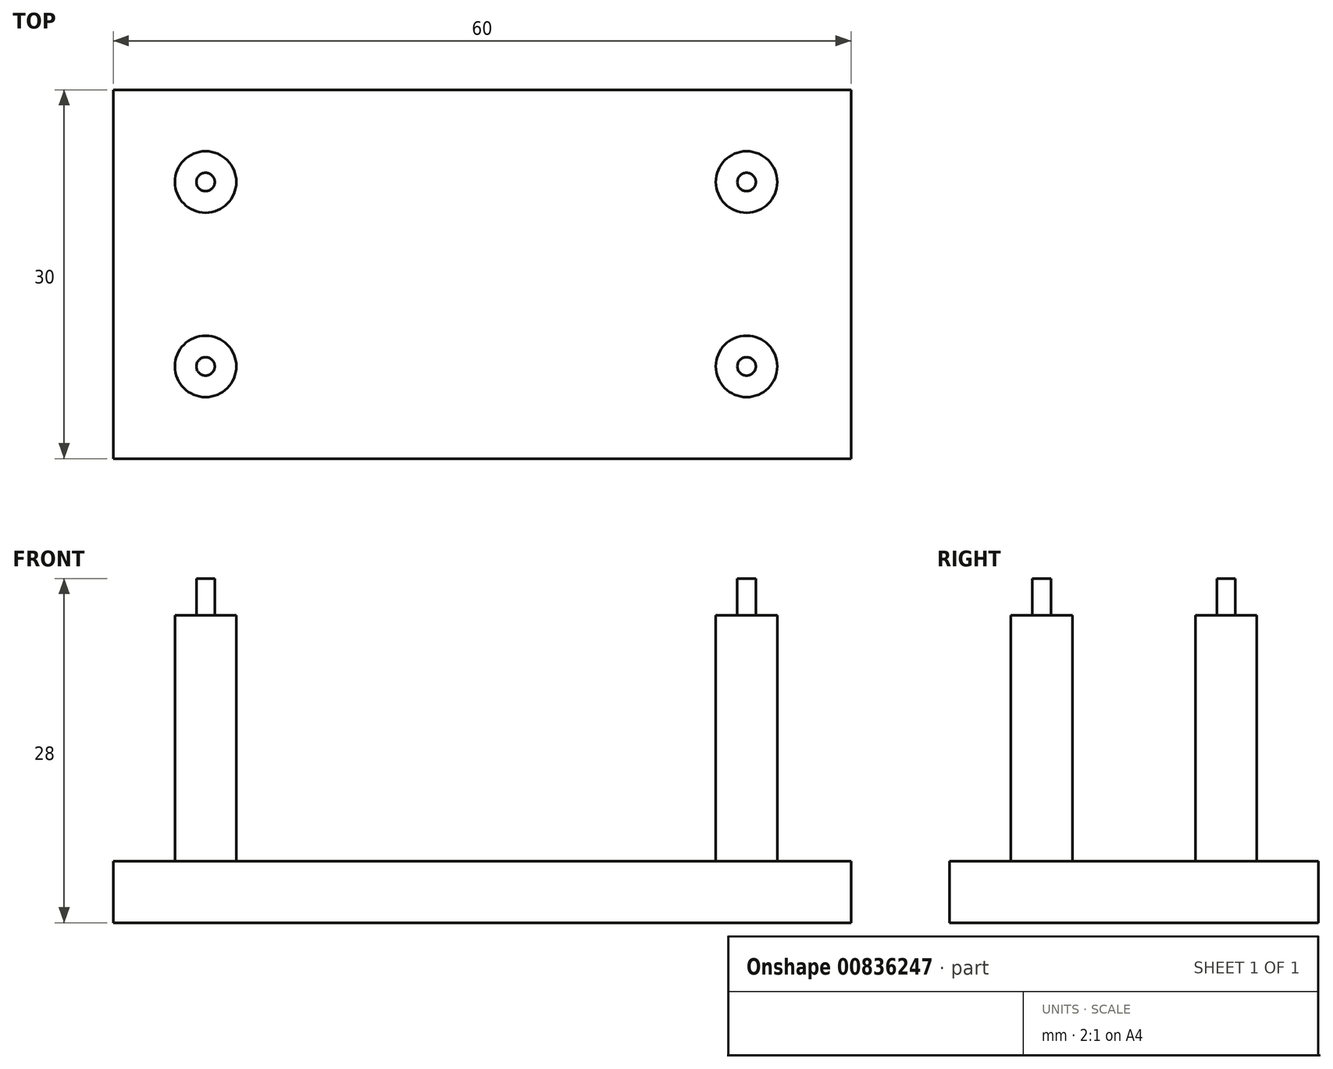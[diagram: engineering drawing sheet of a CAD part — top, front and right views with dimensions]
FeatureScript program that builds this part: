
annotation { "Feature Type Name" : "Feature", "Feature Type Description" : "" }
export const myFeature = defineFeature(function(context is Context, id is Id, definition is map)
    precondition{}
    {
        {
            var Q0;
            Q0=qCreatedBy(makeId("Top.planeOp"),FACE);
            var sketch = newSketch(context, id + "F0", { "sketchPlane" : qUnion([Q0])});
            skLineSegment(sketch, "E0.bottom", {"start": v(-23.52, 12.55) * mm, "end": v(36.48, 12.55) * mm});
            skLineSegment(sketch, "E0.top", {"start": v(-23.52, -17.45) * mm, "end": v(36.48, -17.45) * mm});
            skLineSegment(sketch, "E0.left", {"start": v(-23.52, 12.55) * mm, "end": v(-23.52, -17.45) * mm});
            skLineSegment(sketch, "E0.right", {"start": v(36.48, 12.55) * mm, "end": v(36.48, -17.45) * mm});
            skSolve(sketch);
        }
        {
            var Q0;
            Q0=makeQuery(id+"F0.imprint","IMPRINT",FACE,{"disambiguationData":[TD([[makeQuery(id+"F0.imprint","IMPRINT",EDGE,{"derivedFrom":sQuery(id+"F0.wireOp",EDGE,"E0.bottom")}),-1.0]])]});
            extrude(context, id + "F1", {"entities" : qUnion([Q0]), "depth" : 5 * mm, "offsetDistance" : 25 * mm});
        }
        {
            var Q0;
            Q0=makeQuery(id+"F1.opExtrude","CAP_FACE",FACE,{"disambiguationData":[OSD([sQuery(id+"F0.wireOp",EDGE,"E0.bottom"),sQuery(id+"F0.wireOp",EDGE,"E0.top"),sQuery(id+"F0.wireOp",EDGE,"E0.left"),sQuery(id+"F0.wireOp",EDGE,"E0.right")])],"isStart":false});
            var sketch = newSketch(context, id + "F2", { "sketchPlane" : qUnion([Q0])});
            skCircle(sketch, "E1", {"center": v(-16.02, 5.05) * mm, "radius": 2.5 * mm});
            skPoint(sketch, "E1.first.point", {"position": v(-14.18, 6.75) * mm});
            skPoint(sketch, "E1.second.point", {"position": v(-13.52, 5.02) * mm});
            skPoint(sketch, "E1.third.point", {"position": v(-13.52, 5.09) * mm});
            skCircle(sketch, "E2", {"center": v(-16.02, -9.95) * mm, "radius": 2.5 * mm});
            skPoint(sketch, "E2.first.point", {"position": v(-14.15, -8.28) * mm});
            skPoint(sketch, "E2.second.point", {"position": v(-13.52, -9.96) * mm});
            skPoint(sketch, "E2.third.point", {"position": v(-15.95, -12.44) * mm});
            skCircle(sketch, "E3", {"center": v(27.98, 5.05) * mm, "radius": 2.5 * mm});
            skPoint(sketch, "E3.first.point", {"position": v(26.35, 6.95) * mm});
            skPoint(sketch, "E3.second.point", {"position": v(26.84, 2.83) * mm});
            skPoint(sketch, "E3.third.point", {"position": v(27.69, 2.57) * mm});
            skCircle(sketch, "E4", {"center": v(27.98, -9.95) * mm, "radius": 2.5 * mm});
            skPoint(sketch, "E4.first.point", {"position": v(28.05, -12.44) * mm});
            skPoint(sketch, "E4.second.point", {"position": v(26.84, -7.72) * mm});
            skPoint(sketch, "E4.third.point", {"position": v(25.49, -9.86) * mm});
            skSolve(sketch);
        }
        {
            var Q0;
            Q0 = qSketchRegion(id + "F2", true);
            extrude(context, id + "F3", {"entities" : qUnion([Q0]), "operationType" : NewBodyOperationType.ADD, "depth" : 20 * mm, "offsetDistance" : 25 * mm});
        }
        {
            var Q0;
            Q0=makeQuery(id+"F1.opExtrude","CAP_FACE",FACE,{"disambiguationData":[OSD([sQuery(id+"F0.wireOp",EDGE,"E0.bottom"),sQuery(id+"F0.wireOp",EDGE,"E0.top"),sQuery(id+"F0.wireOp",EDGE,"E0.left"),sQuery(id+"F0.wireOp",EDGE,"E0.right")])],"isStart":false});
            var sketch = newSketch(context, id + "F4", { "sketchPlane" : qUnion([Q0])});
            skCircle(sketch, "E5", {"center": v(-16.02, 5.05) * mm, "radius": 0.75 * mm});
            skCircle(sketch, "E6", {"center": v(-16.02, -9.95) * mm, "radius": 0.75 * mm});
            skCircle(sketch, "E7", {"center": v(27.98, 5.05) * mm, "radius": 0.75 * mm});
            skCircle(sketch, "E8", {"center": v(27.98, -9.95) * mm, "radius": 0.75 * mm});
            skSolve(sketch);
        }
        {
            var Q0;
            Q0 = qSketchRegion(id + "F4", true);
            extrude(context, id + "F5", {"entities" : qUnion([Q0]), "operationType" : NewBodyOperationType.ADD, "depth" : 23 * mm, "offsetDistance" : 25 * mm});
        }
    });
